# Revit family: Toilet-Elongated-DXV-Modulus-D23040A000.415
name_source: partatom
category: Plumbing Fixtures
revit_build: Autodesk Revit 2014 (Build: 20130308_1515(x64)
units: mm (PartAtom-declared; Revit-internal decimal feet)

## types (1)
- D23040A000.415
    5026A10G.415 Toilet Seat = Yes
    Assembly Code = D2010110
    Bowl Shape = Elongated
    CW Connection = Yes
    CWFU = 10
    Cold Water Connection Diameter = 1 1/2"
    Cold Water Connection Radius = 3/4"
    Default Elevation = 15"
    Description = DXV Modulus Wall-Mount Dual Flush Toilet
    Finish = Vitreous China-DXV-415-Canvas White
    Flush Rate = 1.6-0.8 gpf (6.0-3.0 Lpf)
    HW Connection = No
    HWFU = 0
    Height = 13 3/4"
    Installation Type = Wall Mounted
    Length = 22"
    Manufacturer = DXV
    Material = Vitreous China-DXV-415-Canvas White
    Model = D23040A000.415
    Price = Prices may vary. Please consult Manufacturer Representative for most up-to-date price list.
    Product Documentation Link = https://dxv01.blob.core.windows.net
    Product Page URL = https://www.dxv.com
    URL = https://www.dxv.com
    Vent Connection = No
    WFU = 10
    Waste Connection = Yes
    Waste Connection Diameter = 2 1/4"
    Waste Connection Radius = 1 1/8"
    Width = 14 3/16"

## geometry (parser evidence)
native form markers: Sweep x2
no freeform markers — native parametric forms only
